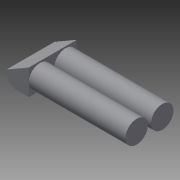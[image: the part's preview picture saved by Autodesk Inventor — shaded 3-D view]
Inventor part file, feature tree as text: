
AUTODESK INVENTOR PART (.ipt)
format: ipt  version: 2015 SP1 (Build 190203100, 203)  size: 96,256 bytes
history: native  units: in
note: dims shown in document units (in); Inventor stores cm internally (conversion verified against a paired STEP export)
features: extrude x2, sketch x2
ambient origin geometry x8: Origin, YZ Plane, XZ Plane, XY Plane, X Axis, Y Axis, Z Axis, Center Point
bodies: Solid1 (feature_tree)
feature tree (4):
  extrude  "Extrusion1"  TaperAngle=60.0deg  [1 undecoded]
  extrude  "Extrusion2"  Depth=3.5in
  sketch  "Sketch1"  dims[d1=8.0in d2=60.0deg]
  sketch  "Sketch2"  dims[d3=8.0in d4=3.5in d5=15.0in d6=0.0in d7=7.0in d8=7.0in d9=30.2in d10=0.0in]
note: 1 required parameter value undecoded (feature->parameter linkage not recoverable at this tier; creation-order binding heuristic only, values carry confidence <= 0.55)
